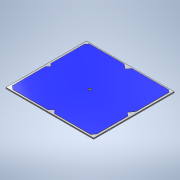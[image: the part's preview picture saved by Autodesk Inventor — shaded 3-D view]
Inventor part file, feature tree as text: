
AUTODESK INVENTOR PART (.ipt)
format: ipt  version: 2020 (Build 240168000, 168)  size: 143,872 bytes
history: native  units: mm
features: extrude x2, sketch x2, other x1
ambient origin geometry x8: Origin, YZ Plane, XZ Plane, XY Plane, X Axis, Y Axis, Z Axis, Center Point
bodies: Body1 (feature_tree)
feature tree (5):
  other  "Sólido1"
  extrude  "Extrusión1"  Depth=180.0mm
  extrude  "Extrusión2"  TaperAngle=135.0deg  [1 undecoded]
  sketch  "Boceto1"  dims[d2=165.0mm d3=180.0mm]
  sketch  "Boceto3"  dims[d4=5.0mm d5=0.0mm d7=135.0deg d8=135.0deg d9=45.0deg d10=1.0mm d11=0.0mm]
note: 1 required parameter value undecoded (feature->parameter linkage not recoverable at this tier; creation-order binding heuristic only, values carry confidence <= 0.55)
